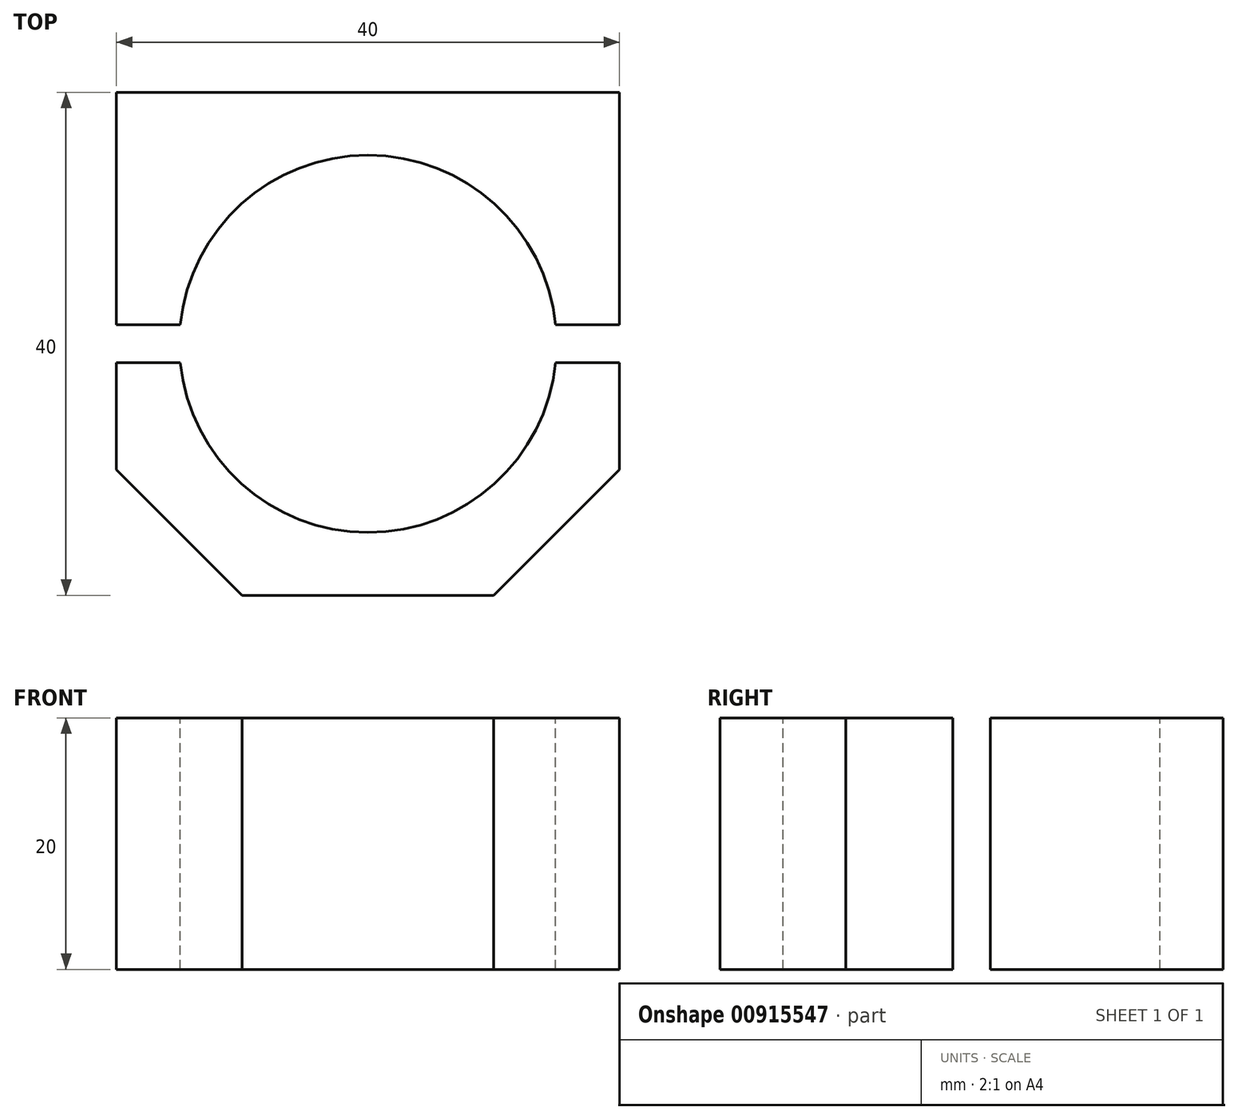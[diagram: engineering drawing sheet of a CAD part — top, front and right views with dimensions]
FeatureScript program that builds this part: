
annotation { "Feature Type Name" : "Feature", "Feature Type Description" : "" }
export const myFeature = defineFeature(function(context is Context, id is Id, definition is map)
    precondition{}
    {
        {
            var Q0;
            Q0=qCreatedBy(makeId("Top.planeOp"),FACE);
            var sketch = newSketch(context, id + "F0", { "sketchPlane" : qUnion([Q0])});
            skLineSegment(sketch, "E0.bottom", {"start": v(20, -20) * mm, "end": v(-20, -20) * mm});
            skLineSegment(sketch, "E0.top", {"start": v(20, 20) * mm, "end": v(-20, 20) * mm});
            skLineSegment(sketch, "E0.left", {"start": v(20, -20) * mm, "end": v(20, 20) * mm});
            skLineSegment(sketch, "E0.right", {"start": v(-20, -20) * mm, "end": v(-20, 20) * mm});
            skPoint(sketch, "E0.middle", {"position": v(0, 0) * mm});
            skSolve(sketch);
        }
        {
            var Q0;
            Q0=makeQuery(id+"F0.imprint","IMPRINT",FACE,{"disambiguationData":[TD([[makeQuery(id+"F0.imprint","IMPRINT",EDGE,{"derivedFrom":sQuery(id+"F0.wireOp",EDGE,"E0.bottom")}),-1.0]])]});
            extrude(context, id + "F1", {"entities" : qUnion([Q0]), "depth" : 20 * mm, "offsetDistance" : 25 * mm});
        }
        {
            var Q0;
            Q0=makeQuery(id+"F1.opExtrude","CAP_FACE",FACE,{"disambiguationData":[OSD([sQuery(id+"F0.wireOp",EDGE,"E0.bottom"),sQuery(id+"F0.wireOp",EDGE,"E0.top"),sQuery(id+"F0.wireOp",EDGE,"E0.left"),sQuery(id+"F0.wireOp",EDGE,"E0.right")])],"isStart":false});
            var sketch = newSketch(context, id + "F2", { "sketchPlane" : qUnion([Q0])});
            skPoint(sketch, "E1", {"position": v(0, 0) * mm});
            skSolve(sketch);
        }
        {
            var Q0;
            Q0=sQuery(id+"F2.wireOp",VERTEX,"E1");
            var Q1;
            Q1=makeQuery(id+"F1.opExtrude","SWEPT_BODY",BODY,{"disambiguationData":[OSD([sQuery(id+"F0.wireOp",EDGE,"E0.bottom"),sQuery(id+"F0.wireOp",EDGE,"E0.top"),sQuery(id+"F0.wireOp",EDGE,"E0.left"),sQuery(id+"F0.wireOp",EDGE,"E0.right")])]});
            hole(context, id + "F3", {"style" : HoleStyle.SIMPLE, "endStyle" : HoleEndStyle.THROUGH, "holeDiameter" : 30 * mm, "majorDiameter" : 5 * mm, "isTappedThrough" : true, "tappedDepth" : 12 * mm, "tapClearance" : 3, "locations" : qUnion([Q0]), "scope" : qUnion([Q1])});
        }
        {
            var Q0;
            Q0=makeQuery(id+"F1.opExtrude","CAP_FACE",FACE,{"disambiguationData":[OSD([sQuery(id+"F0.wireOp",EDGE,"E0.bottom"),sQuery(id+"F0.wireOp",EDGE,"E0.top"),sQuery(id+"F0.wireOp",EDGE,"E0.left"),sQuery(id+"F0.wireOp",EDGE,"E0.right")])],"isStart":false});
            var sketch = newSketch(context, id + "F4", { "sketchPlane" : qUnion([Q0])});
            skLineSegment(sketch, "E2.bottom", {"start": v(20, -1.5) * mm, "end": v(-20, -1.5) * mm});
            skLineSegment(sketch, "E2.top", {"start": v(20, 1.5) * mm, "end": v(-20, 1.5) * mm});
            skLineSegment(sketch, "E2.left", {"start": v(20, -1.5) * mm, "end": v(20, 1.5) * mm});
            skLineSegment(sketch, "E2.right", {"start": v(-20, -1.5) * mm, "end": v(-20, 1.5) * mm});
            skPoint(sketch, "E2.middle", {"position": v(0, 0) * mm});
            skSolve(sketch);
        }
        {
            var Q0;
            {var subQ0=sQuery(id+"F4.wireOp",EDGE,"E2.right");Q0=makeQuery(id+"F4.imprint","IMPRINT",FACE,{"disambiguationData":[TD([[makeQuery(id+"F4.imprint","IMPRINT",EDGE,{"derivedFrom":subQ0}),-1.0]])]});}
            var Q1;
            {var subQ0=sQuery(id+"F4.wireOp",EDGE,"E2.left");Q1=makeQuery(id+"F4.imprint","IMPRINT",FACE,{"disambiguationData":[TD([[makeQuery(id+"F4.imprint","IMPRINT",EDGE,{"derivedFrom":subQ0}),1.0]])]});}
            extrude(context, id + "F5", {"entities" : qUnion([Q0, Q1]), "operationType" : NewBodyOperationType.REMOVE, "oppositeDirection" : true, "depth" : 25 * mm, "offsetDistance" : 25 * mm});
        }
        {
            var Q0;
            Q0=makeQuery(id+"F1.opExtrude","SWEPT_EDGE",EDGE,{"disambiguationData":[OSD([sQuery(id+"F0.wireOp",EDGE,"E0.bottom"),sQuery(id+"F0.wireOp",EDGE,"E0.right")])]});
            var Q1;
            Q1=makeQuery(id+"F1.opExtrude","SWEPT_EDGE",EDGE,{"disambiguationData":[OSD([sQuery(id+"F0.wireOp",EDGE,"E0.bottom"),sQuery(id+"F0.wireOp",EDGE,"E0.left")])]});
            chamfer(context, id + "F6", {"entities" : qUnion([Q0, Q1]), "width" : 10 * mm, "tangentPropagation" : true});
        }
    });
